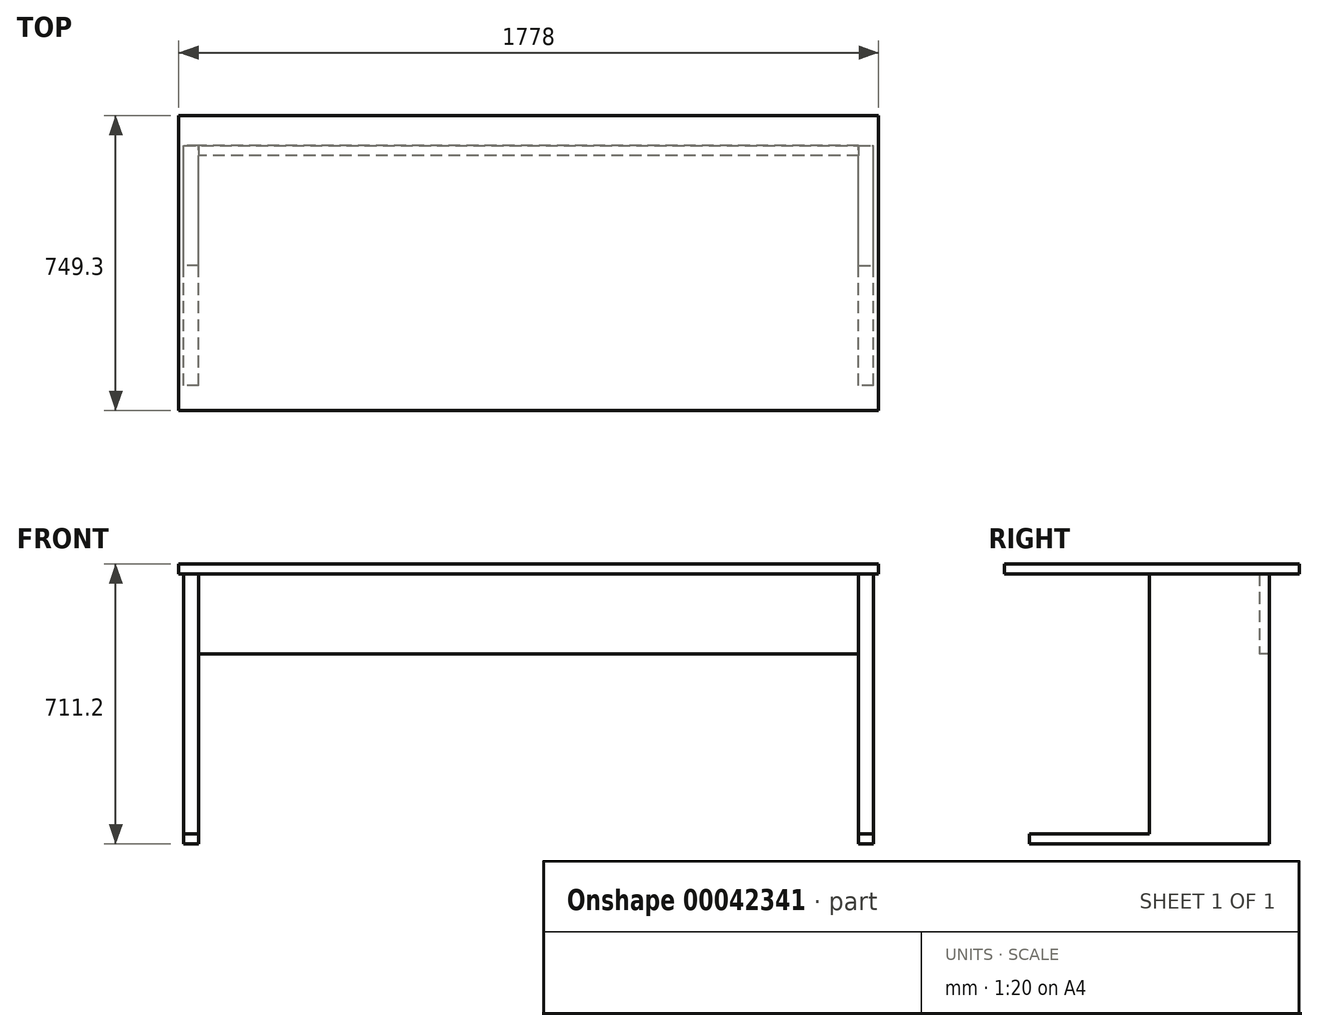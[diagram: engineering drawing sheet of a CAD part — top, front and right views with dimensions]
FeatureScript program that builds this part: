
annotation { "Feature Type Name" : "Feature", "Feature Type Description" : "" }
export const myFeature = defineFeature(function(context is Context, id is Id, definition is map)
    precondition{}
    {
        {
            var Q0;
            Q0=qCreatedBy(makeId("Top.planeOp"),FACE);
            var sketch = newSketch(context, id + "F0", { "sketchPlane" : qUnion([Q0])});
            skLineSegment(sketch, "E0.rect.bottom", {"start": v(889, 374.65) * mm, "end": v(-889, 374.65) * mm});
            skLineSegment(sketch, "E0.rect.top", {"start": v(889, -374.65) * mm, "end": v(-889, -374.65) * mm});
            skLineSegment(sketch, "E0.rect.left", {"start": v(889, 374.65) * mm, "end": v(889, -374.65) * mm});
            skLineSegment(sketch, "E0.rect.right", {"start": v(-889, 374.65) * mm, "end": v(-889, -374.65) * mm});
            skPoint(sketch, "E0.rect.middle", {"position": v(0, 0) * mm});
            skSolve(sketch);
        }
        {
            var Q0;
            Q0=makeQuery(id+"F0.imprint","IMPRINT",FACE,{"disambiguationData":[TD([[makeQuery(id+"F0.imprint","IMPRINT",EDGE,{"derivedFrom":sQuery(id+"F0.wireOp",EDGE,"E0.rect.bottom")}),1.0]])]});
            extrude(context, id + "F1", {"entities" : qUnion([Q0]), "oppositeDirection" : true, "depth" : 25.4 * mm});
        }
        {
            var Q0;
            Q0=makeQuery(id+"F1.opExtrude","CAP_FACE",FACE,{"disambiguationData":[OSD([sQuery(id+"F0.wireOp",EDGE,"E0.rect.bottom"),sQuery(id+"F0.wireOp",EDGE,"E0.rect.top"),sQuery(id+"F0.wireOp",EDGE,"E0.rect.left"),sQuery(id+"F0.wireOp",EDGE,"E0.rect.right")])],"isStart":false});
            var sketch = newSketch(context, id + "F2", { "sketchPlane" : qUnion([Q0])});
            skLineSegment(sketch, "E1.bottom", {"start": v(838.2, 6.35) * mm, "end": v(876.3, 6.35) * mm});
            skLineSegment(sketch, "E1.top", {"start": v(838.2, -298.45) * mm, "end": v(876.3, -298.45) * mm});
            skLineSegment(sketch, "E1.left", {"start": v(838.2, 6.35) * mm, "end": v(838.2, -298.45) * mm});
            skLineSegment(sketch, "E1.right", {"start": v(876.3, 6.35) * mm, "end": v(876.3, -298.45) * mm});
            skLineSegment(sketch, "E2.MirrorCS", {"start": v(-838.2, -298.45) * mm, "end": v(-876.3, -298.45) * mm});
            skLineSegment(sketch, "E3.MirrorCS", {"start": v(-838.2, 6.35) * mm, "end": v(-876.3, 6.35) * mm});
            skLineSegment(sketch, "E4.MirrorCS", {"start": v(-838.2, 6.35) * mm, "end": v(-838.2, -298.45) * mm});
            skLineSegment(sketch, "E5.MirrorCS", {"start": v(-876.3, 6.35) * mm, "end": v(-876.3, -298.45) * mm});
            skSolve(sketch);
        }
        {
            var Q0;
            Q0=qSketchRegion(id+"F2",true);
            extrude(context, id + "F3", {"entities" : qUnion([Q0]), "operationType" : NewBodyOperationType.ADD, "depth" : 660.4 * mm});
        }
        {
            var Q0;
            Q0=makeQuery(id+"F3.opExtrude","CAP_FACE",FACE,{"disambiguationData":[OSD([sQuery(id+"F2.wireOp",EDGE,"E1.bottom"),sQuery(id+"F2.wireOp",EDGE,"E1.top"),sQuery(id+"F2.wireOp",EDGE,"E1.left"),sQuery(id+"F2.wireOp",EDGE,"E1.right")])],"isStart":false});
            var sketch = newSketch(context, id + "F4", { "sketchPlane" : qUnion([Q0])});
            skLineSegment(sketch, "E6.bottom", {"start": v(876.3, -298.45) * mm, "end": v(838.2, -298.45) * mm});
            skLineSegment(sketch, "E6.top", {"start": v(876.3, 311.15) * mm, "end": v(838.2, 311.15) * mm});
            skLineSegment(sketch, "E6.left", {"start": v(876.3, -298.45) * mm, "end": v(876.3, 311.15) * mm});
            skLineSegment(sketch, "E6.right", {"start": v(838.2, -298.45) * mm, "end": v(838.2, 311.15) * mm});
            skSolve(sketch);
        }
        {
            var Q0;
            Q0=makeQuery(id+"F3.opExtrude","CAP_FACE",FACE,{"disambiguationData":[OSD([sQuery(id+"F2.wireOp",EDGE,"E2.MirrorCS"),sQuery(id+"F2.wireOp",EDGE,"E3.MirrorCS"),sQuery(id+"F2.wireOp",EDGE,"E4.MirrorCS"),sQuery(id+"F2.wireOp",EDGE,"E5.MirrorCS")])],"isStart":false});
            var sketch = newSketch(context, id + "F5", { "sketchPlane" : qUnion([Q0])});
            skLineSegment(sketch, "E7.bottom", {"start": v(-838.2, -298.45) * mm, "end": v(-876.3, -298.45) * mm});
            skLineSegment(sketch, "E7.top", {"start": v(-838.2, 311.15) * mm, "end": v(-876.3, 311.15) * mm});
            skLineSegment(sketch, "E7.left", {"start": v(-838.2, -298.45) * mm, "end": v(-838.2, 311.15) * mm});
            skLineSegment(sketch, "E7.right", {"start": v(-876.3, -298.45) * mm, "end": v(-876.3, 311.15) * mm});
            skSolve(sketch);
        }
        {
            var Q0;
            Q0=qSketchRegion(id+"F5",true);
            var Q1;
            Q1=qSketchRegion(id+"F4",true);
            extrude(context, id + "F6", {"entities" : qUnion([Q0, Q1]), "operationType" : NewBodyOperationType.ADD, "depth" : 25.4 * mm});
        }
        {
            var Q0;
            Q0=makeQuery(id+"F6.boolean.opBoolean","MERGE",FACE,{"derivedFrom":[makeQuery(id+"F3.opExtrude","SWEPT_FACE",FACE,{"disambiguationData":[OSD([sQuery(id+"F2.wireOp",EDGE,"E4.MirrorCS")])]}),makeQuery(id+"F6.opExtrude","SWEPT_FACE",FACE,{"disambiguationData":[OSD([sQuery(id+"F5.wireOp",EDGE,"E7.left")])]})]});
            var sketch = newSketch(context, id + "F7", { "sketchPlane" : qUnion([Q0])});
            skLineSegment(sketch, "E8.bottom", {"start": v(298.45, -25.4) * mm, "end": v(273.05, -25.4) * mm});
            skLineSegment(sketch, "E8.top", {"start": v(298.45, -228.6) * mm, "end": v(273.05, -228.6) * mm});
            skLineSegment(sketch, "E8.left", {"start": v(298.45, -25.4) * mm, "end": v(298.45, -228.6) * mm});
            skLineSegment(sketch, "E8.right", {"start": v(273.05, -25.4) * mm, "end": v(273.05, -228.6) * mm});
            skSolve(sketch);
        }
        {
            var Q0;
            Q0=qSketchRegion(id+"F7",true);
            extrude(context, id + "F8", {"entities" : qUnion([Q0]), "operationType" : NewBodyOperationType.ADD, "endBound" : BoundingType.UP_TO_NEXT, "depth" : 25.4 * mm});
        }
    });
